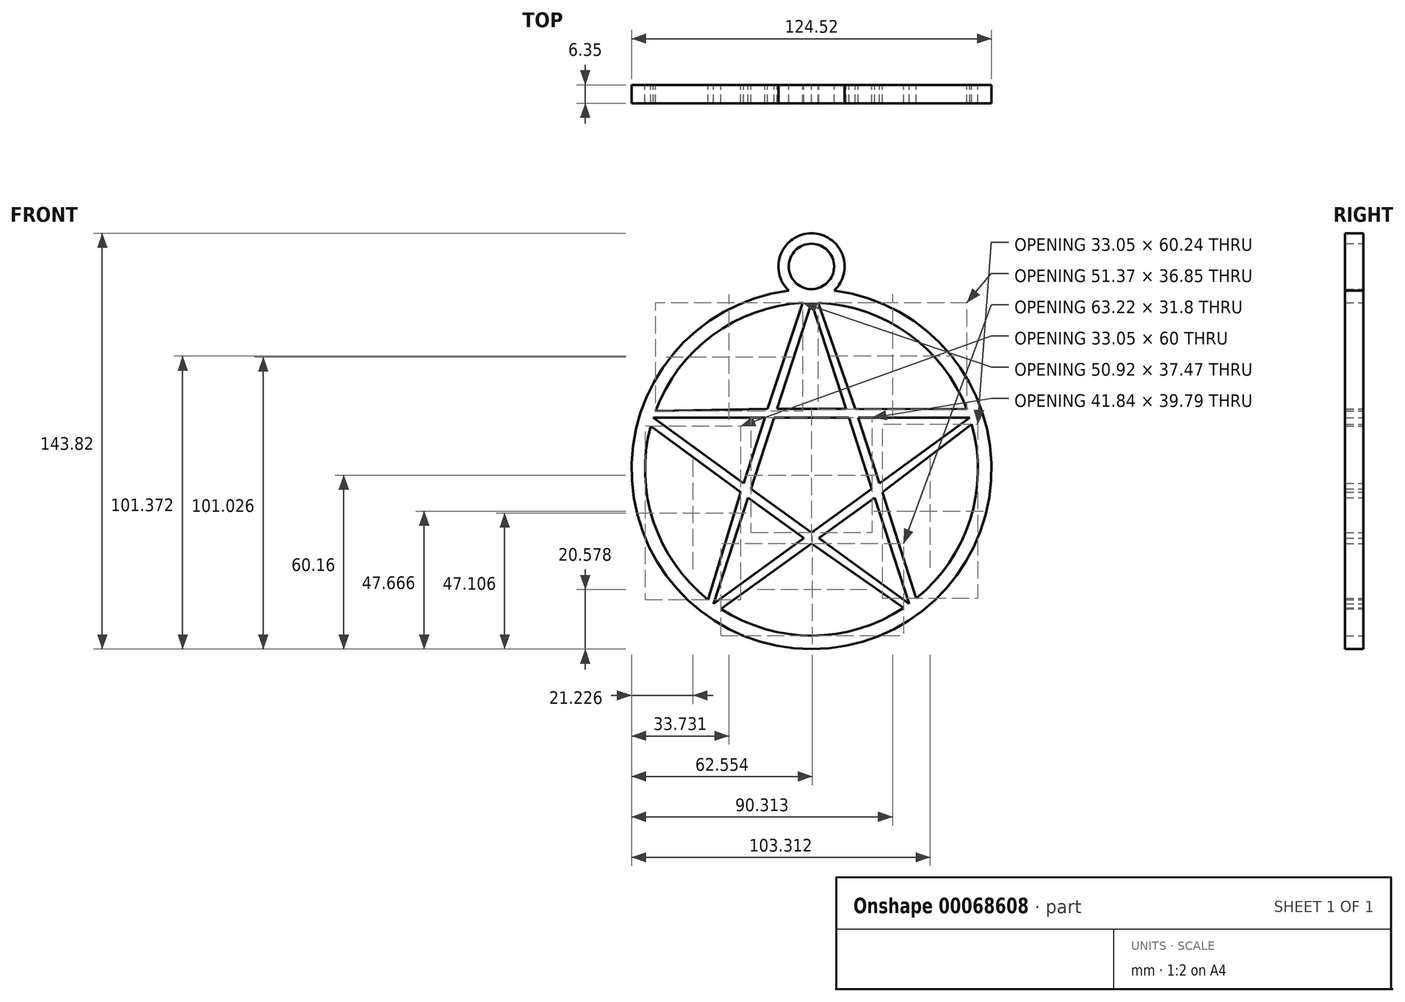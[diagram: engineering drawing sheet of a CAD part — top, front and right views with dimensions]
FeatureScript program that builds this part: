
annotation { "Feature Type Name" : "Feature", "Feature Type Description" : "" }
export const myFeature = defineFeature(function(context is Context, id is Id, definition is map)
    precondition{}
    {
        {
            var Q0;
            Q0=qCreatedBy(makeId("Front.planeOp"),FACE);
            var sketch = newSketch(context, id + "F0", { "sketchPlane" : qUnion([Q0])});
            skCircle(sketch, "E0", {"center": v(0, 0) * mm, "radius": 57.58 * mm});
            skCircle(sketch, "E1.cCircle", {"center": v(0, 0) * mm, "radius": 57.58 * mm, "construction": true});
            skLineSegment(sketch, "E2", {"start": v(0, 57.58) * mm, "end": v(33.85, -46.59) * mm});
            skLineSegment(sketch, "E3", {"start": v(-54.77, 17.8) * mm, "end": v(33.85, -46.59) * mm});
            skLineSegment(sketch, "E4", {"start": v(-54.77, 17.8) * mm, "end": v(54.77, 17.8) * mm});
            skLineSegment(sketch, "E5", {"start": v(54.77, 17.8) * mm, "end": v(-33.85, -46.59) * mm});
            skLineSegment(sketch, "E6", {"start": v(-33.85, -46.59) * mm, "end": v(0, 57.58) * mm});
            skCircle(sketch, "E7", {"center": v(0, 0) * mm, "radius": 62.26 * mm});
            skLineSegment(sketch, "E8.0", {"start": v(-15.18, 20.84) * mm, "end": v(15.13, 20.88) * mm});
            skLineSegment(sketch, "E8.1", {"start": v(15.13, 20.88) * mm, "end": v(24.53, -7.94) * mm});
            skLineSegment(sketch, "E8.2", {"start": v(24.53, -7.94) * mm, "end": v(0.03, -25.78) * mm});
            skLineSegment(sketch, "E8.3", {"start": v(0.03, -25.78) * mm, "end": v(-24.5, -8) * mm});
            skLineSegment(sketch, "E8.4", {"start": v(-24.5, -8) * mm, "end": v(-15.18, 20.84) * mm});
            skLineSegment(sketch, "E9", {"start": v(-15.18, 20.84) * mm, "end": v(-3.07, 57.5) * mm});
            skLineSegment(sketch, "E10", {"start": v(-15.18, 20.84) * mm, "end": v(-53.99, 20.03) * mm});
            skLineSegment(sketch, "E11", {"start": v(-55.64, 14.85) * mm, "end": v(-24.5, -8) * mm});
            skLineSegment(sketch, "E12", {"start": v(0.03, -25.78) * mm, "end": v(-31.31, -48.32) * mm});
            skLineSegment(sketch, "E13", {"start": v(0.03, -25.78) * mm, "end": v(31.9, -47.94) * mm});
            skLineSegment(sketch, "E14", {"start": v(24.53, -7.94) * mm, "end": v(36.28, -44.71) * mm});
            skLineSegment(sketch, "E15", {"start": v(24.53, -7.94) * mm, "end": v(55.45, 15.53) * mm});
            skLineSegment(sketch, "E16", {"start": v(15.13, 20.88) * mm, "end": v(53.74, 20.69) * mm});
            skLineSegment(sketch, "E17", {"start": v(15.13, 20.88) * mm, "end": v(2.37, 57.53) * mm});
            skLineSegment(sketch, "E18", {"start": v(-24.5, -8) * mm, "end": v(-35.73, -45.16) * mm});
            skCircle(sketch, "E19", {"center": v(0, 70.11) * mm, "radius": 11.45 * mm});
            skCircle(sketch, "E20", {"center": v(0, 70.11) * mm, "radius": 7.85 * mm});
            skSolve(sketch);
        }
        {
            var Q0;
            {var subQ3=sQuery(id+"F0.wireOp",EDGE,"E15");Q0=makeQuery(id+"F0.imprint","IMPRINT",FACE,{"disambiguationData":[TD([[makeQuery(id+"F0.imprint","IMPRINT",EDGE,{"derivedFrom":subQ3}),1.0]])]});}
            var Q1;
            {var subQ3=sQuery(id+"F0.wireOp",EDGE,"E16");Q1=makeQuery(id+"F0.imprint","IMPRINT",FACE,{"disambiguationData":[TD([[makeQuery(id+"F0.imprint","IMPRINT",EDGE,{"derivedFrom":subQ3}),-1.0]])]});}
            var Q2;
            {var subQ2=sQuery(id+"F0.wireOp",EDGE,"E0");var subQ14=makeQuery(id+"F0.imprint","INTERSECT",VERTEX,{"derivedFrom":[subQ2,sQuery(id+"F0.wireOp",EDGE,"E16")]});Q2=makeQuery(id+"F0.imprint","IMPRINT",FACE,{"disambiguationData":[TD([[makeQuery(id+"F0.imprint","IMPRINT",EDGE,{"disambiguationData":[TD([[subQ14,-1.0]])],"derivedFrom":subQ2}),-1.0]])]});}
            var Q3;
            {var subQ0=sQuery(id+"F0.wireOp",EDGE,"E5");var subQ1=sQuery(id+"F0.wireOp",EDGE,"E2");var subQ2=makeQuery(id+"F0.imprint","INTERSECT",VERTEX,{"derivedFrom":[subQ1,subQ0]});Q3=makeQuery(id+"F0.imprint","IMPRINT",FACE,{"disambiguationData":[TD([[makeQuery(id+"F0.imprint","IMPRINT",EDGE,{"disambiguationData":[TD([[subQ2,-1.0]])],"derivedFrom":subQ1}),1.0]])]});}
            var Q4;
            {var subQ0=sQuery(id+"F0.wireOp",EDGE,"E4");var subQ1=sQuery(id+"F0.wireOp",EDGE,"E2");var subQ2=makeQuery(id+"F0.imprint","INTERSECT",VERTEX,{"derivedFrom":[subQ1,subQ0]});Q4=makeQuery(id+"F0.imprint","IMPRINT",FACE,{"disambiguationData":[TD([[makeQuery(id+"F0.imprint","IMPRINT",EDGE,{"disambiguationData":[TD([[subQ2,-1.0]])],"derivedFrom":subQ1}),1.0]])]});}
            var Q5;
            {var subQ3=sQuery(id+"F0.wireOp",EDGE,"E14");Q5=makeQuery(id+"F0.imprint","IMPRINT",FACE,{"disambiguationData":[TD([[makeQuery(id+"F0.imprint","IMPRINT",EDGE,{"derivedFrom":subQ3}),-1.0]])]});}
            var Q6;
            {var subQ0=sQuery(id+"F0.wireOp",EDGE,"E5");var subQ1=sQuery(id+"F0.wireOp",EDGE,"E2");var subQ2=makeQuery(id+"F0.imprint","INTERSECT",VERTEX,{"derivedFrom":[subQ1,subQ0]});Q6=makeQuery(id+"F0.imprint","IMPRINT",FACE,{"disambiguationData":[TD([[makeQuery(id+"F0.imprint","IMPRINT",EDGE,{"disambiguationData":[TD([[subQ2,-1.0]])],"derivedFrom":subQ1}),-1.0]])]});}
            var Q7;
            {var subQ3=sQuery(id+"F0.wireOp",EDGE,"E17");Q7=makeQuery(id+"F0.imprint","IMPRINT",FACE,{"disambiguationData":[TD([[makeQuery(id+"F0.imprint","IMPRINT",EDGE,{"derivedFrom":subQ3}),1.0]])]});}
            var Q8;
            {var subQ0=sQuery(id+"F0.wireOp",EDGE,"E8.0");var subQ1=sQuery(id+"F0.wireOp",EDGE,"E2");var subQ2=makeQuery(id+"F0.imprint","INTERSECT",VERTEX,{"derivedFrom":[subQ1,subQ0]});Q8=makeQuery(id+"F0.imprint","IMPRINT",FACE,{"disambiguationData":[TD([[makeQuery(id+"F0.imprint","IMPRINT",EDGE,{"disambiguationData":[TD([[subQ2,-1.0]])],"derivedFrom":subQ1}),1.0]])]});}
            var Q9;
            {var subQ0=sQuery(id+"F0.wireOp",EDGE,"E8.0");var subQ1=sQuery(id+"F0.wireOp",EDGE,"E2");var subQ2=makeQuery(id+"F0.imprint","INTERSECT",VERTEX,{"derivedFrom":[subQ1,subQ0]});Q9=makeQuery(id+"F0.imprint","IMPRINT",FACE,{"disambiguationData":[TD([[makeQuery(id+"F0.imprint","IMPRINT",EDGE,{"disambiguationData":[TD([[subQ2,-1.0]])],"derivedFrom":subQ1}),-1.0]])]});}
            var Q10;
            {var subQ0=sQuery(id+"F0.wireOp",EDGE,"E7");var subQ1=makeQuery(id+"F0.imprint","INTERSECT",VERTEX,{"derivedFrom":[subQ0,sQuery(id+"F0.wireOp",EDGE,"E20")]});Q10=makeQuery(id+"F0.imprint","IMPRINT",FACE,{"disambiguationData":[TD([[makeQuery(id+"F0.imprint","IMPRINT",EDGE,{"disambiguationData":[TD([[subQ1,1.0]])],"derivedFrom":subQ0}),1.0]])]});}
            var Q11;
            {var subQ0=sQuery(id+"F0.wireOp",EDGE,"E20");Q11=makeQuery(id+"F0.imprint","IMPRINT",FACE,{"disambiguationData":[TD([[makeQuery(id+"F0.imprint","IMPRINT",EDGE,{"derivedFrom":subQ0}),-1.0]])]});}
            var Q12;
            {var subQ3=sQuery(id+"F0.wireOp",EDGE,"E9");Q12=makeQuery(id+"F0.imprint","IMPRINT",FACE,{"disambiguationData":[TD([[makeQuery(id+"F0.imprint","IMPRINT",EDGE,{"derivedFrom":subQ3}),-1.0]])]});}
            var Q13;
            {var subQ3=sQuery(id+"F0.wireOp",EDGE,"E10");Q13=makeQuery(id+"F0.imprint","IMPRINT",FACE,{"disambiguationData":[TD([[makeQuery(id+"F0.imprint","IMPRINT",EDGE,{"derivedFrom":subQ3}),1.0]])]});}
            var Q14;
            {var subQ0=sQuery(id+"F0.wireOp",EDGE,"E8.4");var subQ1=sQuery(id+"F0.wireOp",EDGE,"E4");var subQ2=makeQuery(id+"F0.imprint","INTERSECT",VERTEX,{"derivedFrom":[subQ1,subQ0]});Q14=makeQuery(id+"F0.imprint","IMPRINT",FACE,{"disambiguationData":[TD([[makeQuery(id+"F0.imprint","IMPRINT",EDGE,{"disambiguationData":[TD([[subQ2,-1.0]])],"derivedFrom":subQ1}),1.0]])]});}
            var Q15;
            {var subQ0=sQuery(id+"F0.wireOp",EDGE,"E8.4");var subQ1=sQuery(id+"F0.wireOp",EDGE,"E3");var subQ2=makeQuery(id+"F0.imprint","INTERSECT",VERTEX,{"derivedFrom":[subQ1,subQ0]});Q15=makeQuery(id+"F0.imprint","IMPRINT",FACE,{"disambiguationData":[TD([[makeQuery(id+"F0.imprint","IMPRINT",EDGE,{"disambiguationData":[TD([[subQ2,-1.0]])],"derivedFrom":subQ1}),1.0]])]});}
            var Q16;
            {var subQ3=sQuery(id+"F0.wireOp",EDGE,"E11");Q16=makeQuery(id+"F0.imprint","IMPRINT",FACE,{"disambiguationData":[TD([[makeQuery(id+"F0.imprint","IMPRINT",EDGE,{"derivedFrom":subQ3}),1.0]])]});}
            var Q17;
            {var subQ0=sQuery(id+"F0.wireOp",EDGE,"E8.4");var subQ1=sQuery(id+"F0.wireOp",EDGE,"E3");var subQ2=makeQuery(id+"F0.imprint","INTERSECT",VERTEX,{"derivedFrom":[subQ1,subQ0]});Q17=makeQuery(id+"F0.imprint","IMPRINT",FACE,{"disambiguationData":[TD([[makeQuery(id+"F0.imprint","IMPRINT",EDGE,{"disambiguationData":[TD([[subQ2,-1.0]])],"derivedFrom":subQ1}),-1.0]])]});}
            var Q18;
            {var subQ3=sQuery(id+"F0.wireOp",EDGE,"E18");Q18=makeQuery(id+"F0.imprint","IMPRINT",FACE,{"disambiguationData":[TD([[makeQuery(id+"F0.imprint","IMPRINT",EDGE,{"derivedFrom":subQ3}),1.0]])]});}
            var Q19;
            {var subQ0=sQuery(id+"F0.wireOp",EDGE,"E6");var subQ1=sQuery(id+"F0.wireOp",EDGE,"E3");var subQ2=makeQuery(id+"F0.imprint","INTERSECT",VERTEX,{"derivedFrom":[subQ1,subQ0]});Q19=makeQuery(id+"F0.imprint","IMPRINT",FACE,{"disambiguationData":[TD([[makeQuery(id+"F0.imprint","IMPRINT",EDGE,{"disambiguationData":[TD([[subQ2,-1.0]])],"derivedFrom":subQ1}),-1.0]])]});}
            var Q20;
            {var subQ3=sQuery(id+"F0.wireOp",EDGE,"E12");Q20=makeQuery(id+"F0.imprint","IMPRINT",FACE,{"disambiguationData":[TD([[makeQuery(id+"F0.imprint","IMPRINT",EDGE,{"derivedFrom":subQ3}),-1.0]])]});}
            var Q21;
            {var subQ0=sQuery(id+"F0.wireOp",EDGE,"E5");var subQ1=sQuery(id+"F0.wireOp",EDGE,"E3");var subQ2=makeQuery(id+"F0.imprint","INTERSECT",VERTEX,{"derivedFrom":[subQ1,subQ0]});Q21=makeQuery(id+"F0.imprint","IMPRINT",FACE,{"disambiguationData":[TD([[makeQuery(id+"F0.imprint","IMPRINT",EDGE,{"disambiguationData":[TD([[subQ2,-1.0]])],"derivedFrom":subQ1}),-1.0]])]});}
            var Q22;
            {var subQ3=sQuery(id+"F0.wireOp",EDGE,"E13");Q22=makeQuery(id+"F0.imprint","IMPRINT",FACE,{"disambiguationData":[TD([[makeQuery(id+"F0.imprint","IMPRINT",EDGE,{"derivedFrom":subQ3}),1.0]])]});}
            extrude(context, id + "F1", {"entities" : qUnion([Q0, Q1, Q2, Q3, Q4, Q5, Q6, Q7, Q8, Q9, Q10, Q11, Q12, Q13, Q14, Q15, Q16, Q17, Q18, Q19, Q20, Q21, Q22]), "depth" : 6.35 * mm});
        }
    });
